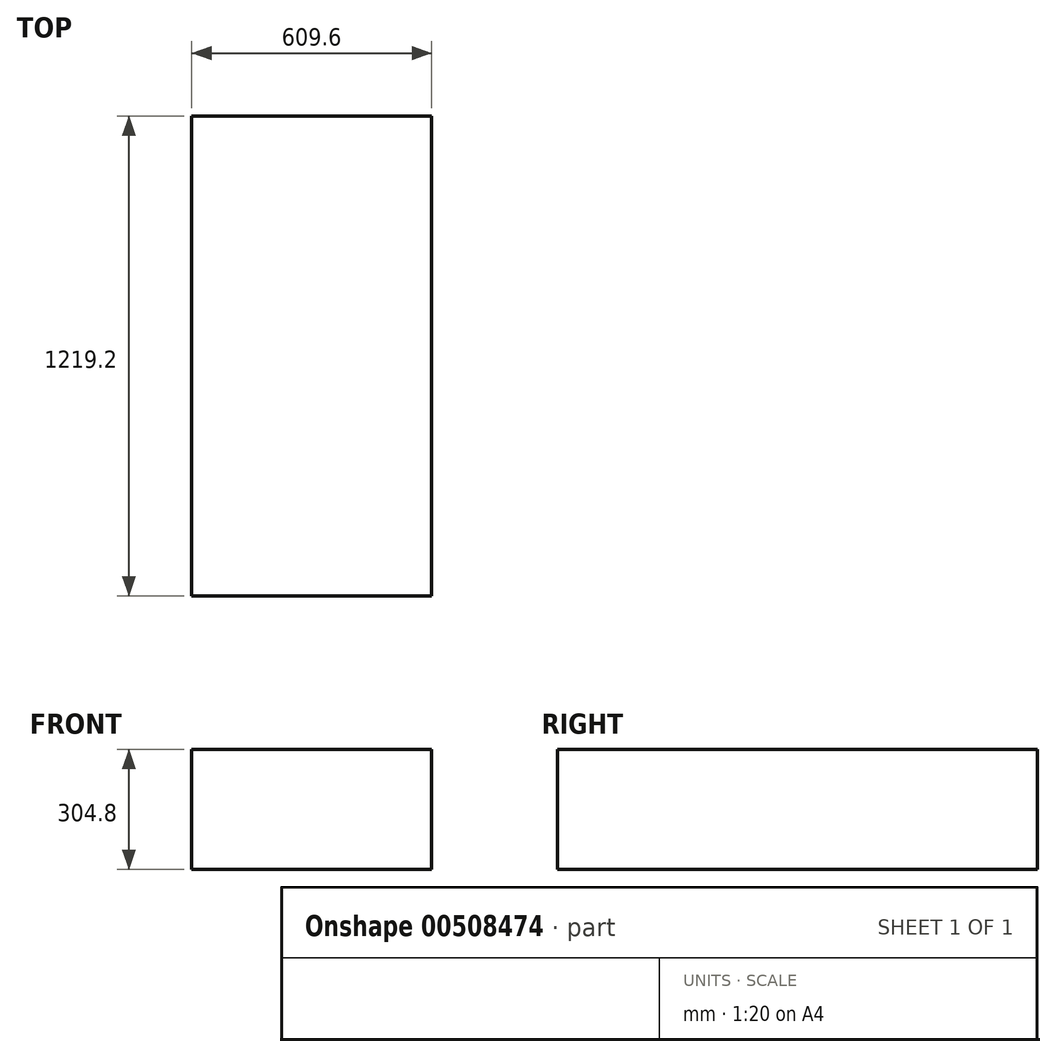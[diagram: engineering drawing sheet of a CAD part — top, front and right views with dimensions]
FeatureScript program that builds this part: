
annotation { "Feature Type Name" : "Feature", "Feature Type Description" : "" }
export const myFeature = defineFeature(function(context is Context, id is Id, definition is map)
    precondition{}
    {
        {
            var Q0;
            Q0=qCreatedBy(makeId("Top.planeOp"),FACE);
            var sketch = newSketch(context, id + "F0", { "sketchPlane" : qUnion([Q0])});
            skLineSegment(sketch, "E0.bottom", {"start": v(-304.8, 609.6) * mm, "end": v(304.8, 609.6) * mm});
            skLineSegment(sketch, "E0.top", {"start": v(-304.8, -609.6) * mm, "end": v(304.8, -609.6) * mm});
            skLineSegment(sketch, "E0.left", {"start": v(-304.8, 609.6) * mm, "end": v(-304.8, -609.6) * mm});
            skLineSegment(sketch, "E0.right", {"start": v(304.8, 609.6) * mm, "end": v(304.8, -609.6) * mm});
            skPoint(sketch, "E0.middle", {"position": v(0, 0) * mm});
            skSolve(sketch);
        }
        {
            var Q0;
            Q0 = qSketchRegion(id + "F0", true);
            extrude(context, id + "F1", {"entities" : qUnion([Q0]), "depth" : 304.8 * mm});
        }
    });
